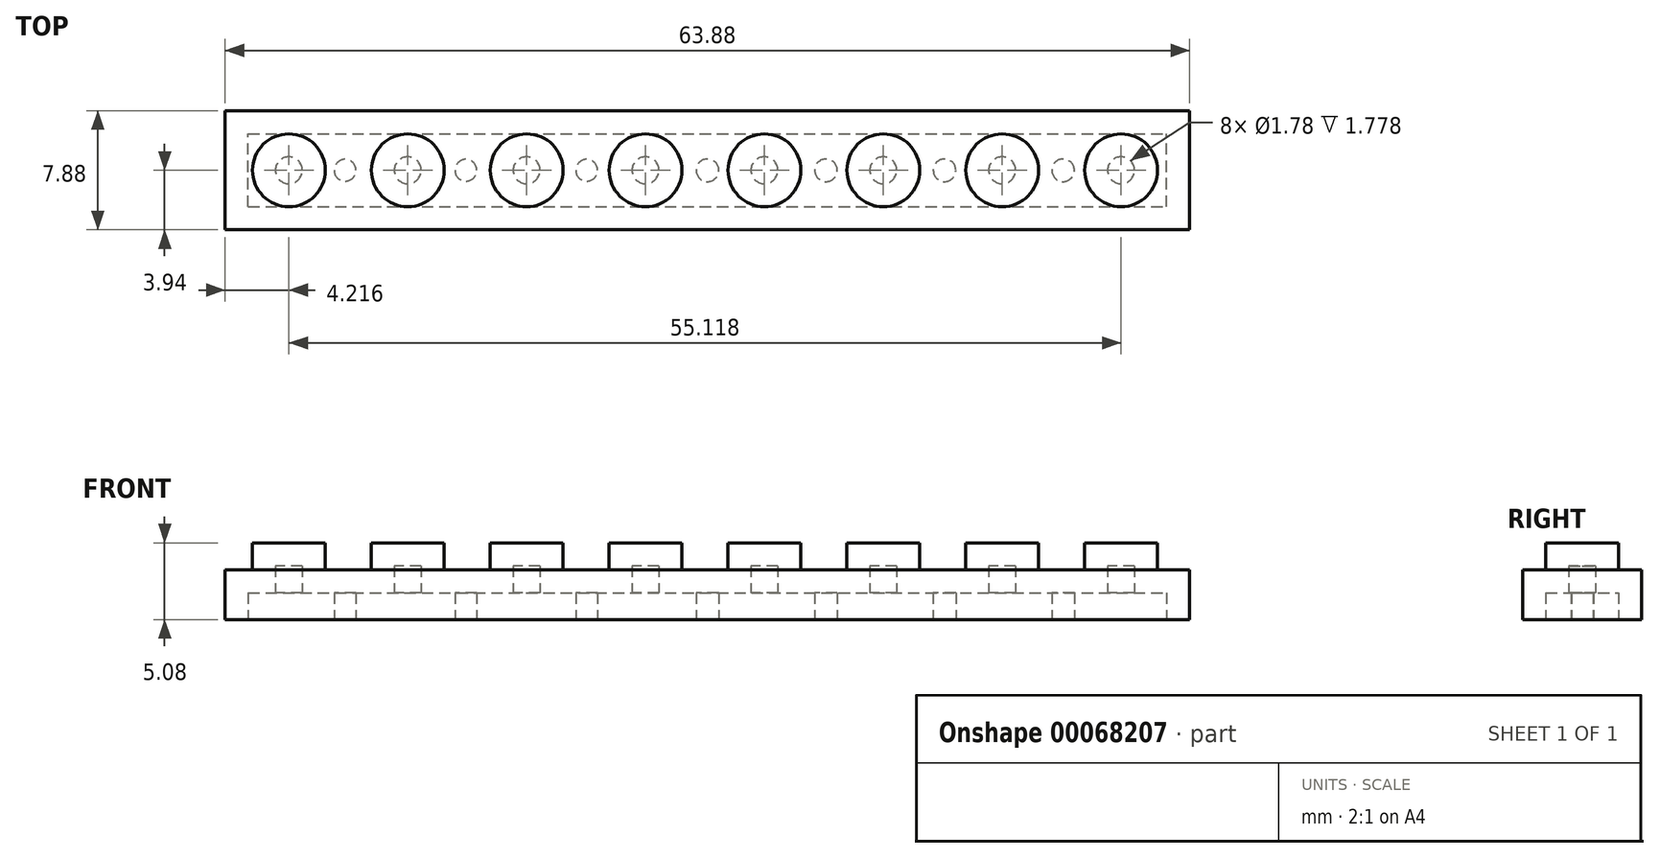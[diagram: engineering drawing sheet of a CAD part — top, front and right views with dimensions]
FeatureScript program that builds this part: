
annotation { "Feature Type Name" : "Feature", "Feature Type Description" : "" }
export const myFeature = defineFeature(function(context is Context, id is Id, definition is map)
    precondition{}
    {
        {
            var Q0;
            Q0=qCreatedBy(makeId("Top.planeOp"),FACE);
            var sketch = newSketch(context, id + "F0", { "sketchPlane" : qUnion([Q0])});
            skLineSegment(sketch, "E0.rect.bottom", {"start": v(-31.94, -3.94) * mm, "end": v(31.94, -3.94) * mm});
            skLineSegment(sketch, "E0.rect.top", {"start": v(-31.94, 3.94) * mm, "end": v(31.94, 3.94) * mm});
            skLineSegment(sketch, "E0.rect.left", {"start": v(-31.94, -3.94) * mm, "end": v(-31.94, 3.94) * mm});
            skLineSegment(sketch, "E0.rect.right", {"start": v(31.94, -3.94) * mm, "end": v(31.94, 3.94) * mm});
            skPoint(sketch, "E0.rect.middle", {"position": v(0, 0) * mm});
            skSolve(sketch);
        }
        {
            var Q0;
            Q0 = qSketchRegion(id + "F0", true);
            extrude(context, id + "F1", {"entities" : qUnion([Q0]), "depth" : 3.3 * mm});
        }
        {
            var Q0;
            Q0=makeQuery(id+"F1.opExtrude","CAP_FACE",FACE,{"disambiguationData":[OSD([sQuery(id+"F0.wireOp",EDGE,"E0.rect.bottom"),sQuery(id+"F0.wireOp",EDGE,"E0.rect.top"),sQuery(id+"F0.wireOp",EDGE,"E0.rect.left"),sQuery(id+"F0.wireOp",EDGE,"E0.rect.right")])],"isStart":false});
            var sketch = newSketch(context, id + "F2", { "sketchPlane" : qUnion([Q0])});
            skLineSegment(sketch, "E1", {"start": v(-31.94, 0) * mm, "end": v(-27.72, 0) * mm});
            skPoint(sketch, "E1.endSnap0", {"position": v(-31.94, 0) * mm});
            skCircle(sketch, "E2", {"center": v(-27.72, 0) * mm, "radius": 2.41 * mm});
            skCircle(sketch, "E3.1.0.0", {"center": v(-19.85, 0) * mm, "radius": 2.41 * mm});
            skCircle(sketch, "E3.2.0.0", {"center": v(-11.98, 0) * mm, "radius": 2.41 * mm});
            skCircle(sketch, "E3.3.0.0", {"center": v(-4.1, 0) * mm, "radius": 2.41 * mm});
            skCircle(sketch, "E3.4.0.0", {"center": v(3.77, 0) * mm, "radius": 2.41 * mm});
            skCircle(sketch, "E3.5.0.0", {"center": v(11.65, 0) * mm, "radius": 2.41 * mm});
            skCircle(sketch, "E3.6.0.0", {"center": v(19.52, 0) * mm, "radius": 2.41 * mm});
            skCircle(sketch, "E3.7.0.0", {"center": v(27.4, 0) * mm, "radius": 2.41 * mm});
            skLineSegment(sketch, "E3.direction1", {"start": v(-27.72, 0) * mm, "end": v(-19.85, 0) * mm, "construction": true});
            skSolve(sketch);
        }
        {
            var Q0;
            Q0=makeQuery(id+"F2.imprint","IMPRINT",FACE,{"disambiguationData":[TD([[makeQuery(id+"F2.imprint","IMPRINT",EDGE,{"derivedFrom":sQuery(id+"F2.wireOp",EDGE,"E2")}),1.0]])]});
            var Q1;
            Q1=makeQuery(id+"F2.imprint","IMPRINT",FACE,{"disambiguationData":[TD([[makeQuery(id+"F2.imprint","IMPRINT",EDGE,{"derivedFrom":sQuery(id+"F2.wireOp",EDGE,"E3.1.0.0")}),1.0]])]});
            var Q2;
            Q2=makeQuery(id+"F2.imprint","IMPRINT",FACE,{"disambiguationData":[TD([[makeQuery(id+"F2.imprint","IMPRINT",EDGE,{"derivedFrom":sQuery(id+"F2.wireOp",EDGE,"E3.2.0.0")}),1.0]])]});
            var Q3;
            Q3=makeQuery(id+"F2.imprint","IMPRINT",FACE,{"disambiguationData":[TD([[makeQuery(id+"F2.imprint","IMPRINT",EDGE,{"derivedFrom":sQuery(id+"F2.wireOp",EDGE,"E3.3.0.0")}),1.0]])]});
            var Q4;
            Q4=makeQuery(id+"F2.imprint","IMPRINT",FACE,{"disambiguationData":[TD([[makeQuery(id+"F2.imprint","IMPRINT",EDGE,{"derivedFrom":sQuery(id+"F2.wireOp",EDGE,"E3.4.0.0")}),1.0]])]});
            var Q5;
            Q5=makeQuery(id+"F2.imprint","IMPRINT",FACE,{"disambiguationData":[TD([[makeQuery(id+"F2.imprint","IMPRINT",EDGE,{"derivedFrom":sQuery(id+"F2.wireOp",EDGE,"E3.5.0.0")}),1.0]])]});
            var Q6;
            Q6=makeQuery(id+"F2.imprint","IMPRINT",FACE,{"disambiguationData":[TD([[makeQuery(id+"F2.imprint","IMPRINT",EDGE,{"derivedFrom":sQuery(id+"F2.wireOp",EDGE,"E3.6.0.0")}),1.0]])]});
            var Q7;
            Q7=makeQuery(id+"F2.imprint","IMPRINT",FACE,{"disambiguationData":[TD([[makeQuery(id+"F2.imprint","IMPRINT",EDGE,{"derivedFrom":sQuery(id+"F2.wireOp",EDGE,"E3.7.0.0")}),1.0]])]});
            var Q8;
            Q8 = qSketchRegion(id + "F0", true);
            extrude(context, id + "F3", {"entities" : qUnion([Q0, Q1, Q2, Q3, Q4, Q5, Q6, Q7, Q8]), "operationType" : NewBodyOperationType.ADD, "depth" : 1.78 * mm});
        }
        {
            var Q0;
            Q0=makeQuery(id+"F1.opExtrude","CAP_FACE",FACE,{"disambiguationData":[OSD([sQuery(id+"F0.wireOp",EDGE,"E0.rect.bottom"),sQuery(id+"F0.wireOp",EDGE,"E0.rect.top"),sQuery(id+"F0.wireOp",EDGE,"E0.rect.left"),sQuery(id+"F0.wireOp",EDGE,"E0.rect.right")])],"isStart":true});
            var sketch = newSketch(context, id + "F4", { "sketchPlane" : qUnion([Q0])});
            skLineSegment(sketch, "E4.rect.bottom", {"start": v(30.42, -2.41) * mm, "end": v(-30.42, -2.41) * mm});
            skLineSegment(sketch, "E4.rect.top", {"start": v(30.42, 2.41) * mm, "end": v(-30.42, 2.41) * mm});
            skLineSegment(sketch, "E4.rect.left", {"start": v(30.42, -2.41) * mm, "end": v(30.42, 2.41) * mm});
            skLineSegment(sketch, "E4.rect.right", {"start": v(-30.42, -2.41) * mm, "end": v(-30.42, 2.41) * mm});
            skPoint(sketch, "E4.rect.middle", {"position": v(0, 0) * mm});
            skSolve(sketch);
        }
        {
            var Q0;
            Q0=makeQuery(id+"F1.opExtrude","CAP_FACE",FACE,{"disambiguationData":[OSD([sQuery(id+"F0.wireOp",EDGE,"E0.rect.bottom"),sQuery(id+"F0.wireOp",EDGE,"E0.rect.top"),sQuery(id+"F0.wireOp",EDGE,"E0.rect.left"),sQuery(id+"F0.wireOp",EDGE,"E0.rect.right")])],"isStart":true});
            shell(context, id + "F5", {"entities" : qUnion([Q0]), "thickness" : 1.52 * mm});
        }
        {
            var Q0;
            Q0=makeQuery(id+"F4.imprint","IMPRINT",FACE,{"disambiguationData":[TD([[makeQuery(id+"F4.imprint","IMPRINT",EDGE,{"derivedFrom":sQuery(id+"F4.wireOp",EDGE,"E4.rect.bottom")}),-1.0]])]});
            var sketch = newSketch(context, id + "F6", { "sketchPlane" : qUnion([Q0])});
            skCircle(sketch, "E5", {"center": v(0, 0) * mm, "radius": 0.75 * mm});
            skCircle(sketch, "E6.1.0.0", {"center": v(7.85, 0) * mm, "radius": 0.75 * mm});
            skCircle(sketch, "E6.2.0.0", {"center": v(15.7, 0) * mm, "radius": 0.75 * mm});
            skCircle(sketch, "E6.3.0.0", {"center": v(23.55, 0) * mm, "radius": 0.75 * mm});
            skLineSegment(sketch, "E6.direction1", {"start": v(0, 0) * mm, "end": v(7.85, 0) * mm, "construction": true});
            skSolve(sketch);
        }
        {
            var Q0;
            Q0=makeQuery(id+"F4.imprint","IMPRINT",FACE,{"disambiguationData":[TD([[makeQuery(id+"F4.imprint","IMPRINT",EDGE,{"derivedFrom":sQuery(id+"F4.wireOp",EDGE,"E4.rect.bottom")}),-1.0]])]});
            var sketch = newSketch(context, id + "F7", { "sketchPlane" : qUnion([Q0])});
            skCircle(sketch, "E7", {"center": v(0, 0) * mm, "radius": 0.72 * mm});
            skCircle(sketch, "E8.1.0.0", {"center": v(-8, 0) * mm, "radius": 0.72 * mm});
            skCircle(sketch, "E8.2.0.0", {"center": v(-16, 0) * mm, "radius": 0.72 * mm});
            skCircle(sketch, "E8.3.0.0", {"center": v(-24, 0) * mm, "radius": 0.72 * mm});
            skLineSegment(sketch, "E8.direction1", {"start": v(0, 0) * mm, "end": v(-8, 0) * mm, "construction": true});
            skSolve(sketch);
        }
        {
            var Q0;
            Q0=makeQuery(id+"F7.imprint","IMPRINT",FACE,{"disambiguationData":[TD([[makeQuery(id+"F7.imprint","IMPRINT",EDGE,{"derivedFrom":sQuery(id+"F7.wireOp",EDGE,"E8.1.0.0")}),1.0]])]});
            var Q1;
            Q1=makeQuery(id+"F7.imprint","IMPRINT",FACE,{"disambiguationData":[TD([[makeQuery(id+"F7.imprint","IMPRINT",EDGE,{"derivedFrom":sQuery(id+"F7.wireOp",EDGE,"E8.3.0.0")}),1.0]])]});
            var Q2;
            Q2=makeQuery(id+"F7.imprint","IMPRINT",FACE,{"disambiguationData":[TD([[makeQuery(id+"F7.imprint","IMPRINT",EDGE,{"derivedFrom":sQuery(id+"F7.wireOp",EDGE,"E8.2.0.0")}),1.0]])]});
            var Q3;
            Q3=makeQuery(id+"F6.imprint","IMPRINT",FACE,{"disambiguationData":[TD([[makeQuery(id+"F6.imprint","IMPRINT",EDGE,{"derivedFrom":sQuery(id+"F6.wireOp",EDGE,"E5")}),1.0]])]});
            var Q4;
            Q4=makeQuery(id+"F6.imprint","IMPRINT",FACE,{"disambiguationData":[TD([[makeQuery(id+"F6.imprint","IMPRINT",EDGE,{"derivedFrom":sQuery(id+"F6.wireOp",EDGE,"E6.1.0.0")}),1.0]])]});
            var Q5;
            Q5=makeQuery(id+"F6.imprint","IMPRINT",FACE,{"disambiguationData":[TD([[makeQuery(id+"F6.imprint","IMPRINT",EDGE,{"derivedFrom":sQuery(id+"F6.wireOp",EDGE,"E6.2.0.0")}),1.0]])]});
            var Q6;
            Q6=makeQuery(id+"F6.imprint","IMPRINT",FACE,{"disambiguationData":[TD([[makeQuery(id+"F6.imprint","IMPRINT",EDGE,{"derivedFrom":sQuery(id+"F6.wireOp",EDGE,"E6.3.0.0")}),1.0]])]});
            extrude(context, id + "F8", {"entities" : qUnion([Q0, Q1, Q2, Q3, Q4, Q5, Q6]), "operationType" : NewBodyOperationType.ADD, "oppositeDirection" : true, "depth" : 3.2 * mm});
        }
    });
